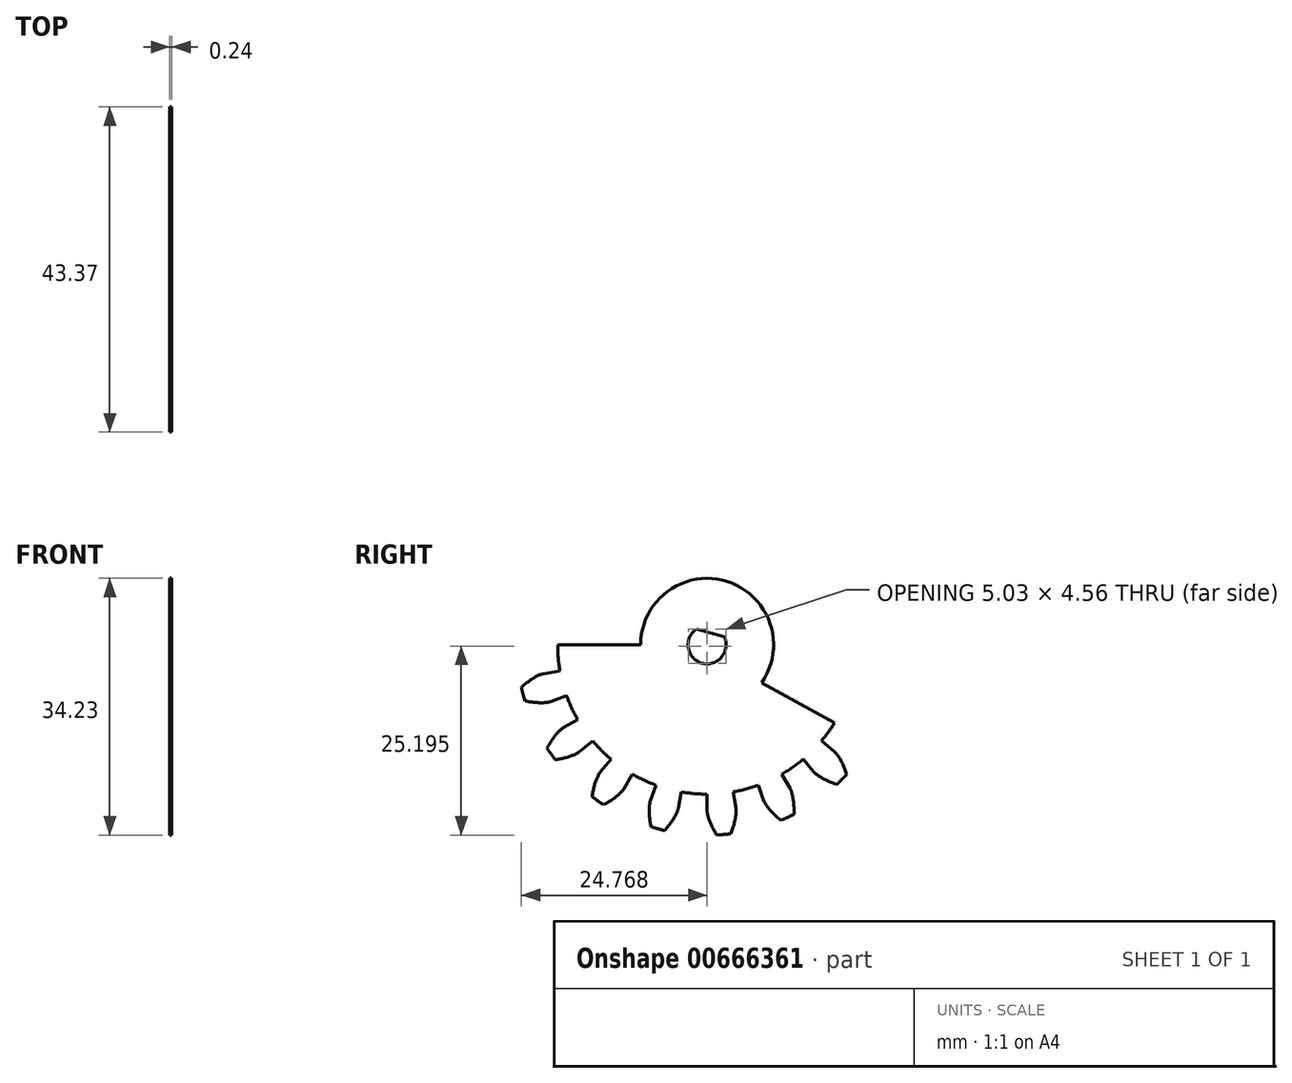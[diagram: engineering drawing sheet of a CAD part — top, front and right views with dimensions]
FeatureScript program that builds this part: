
annotation { "Feature Type Name" : "Feature", "Feature Type Description" : "" }
export const myFeature = defineFeature(function(context is Context, id is Id, definition is map)
    precondition{}
    {
        {
            assignVariable(context, id + "F0", {"name" : "NumberTeeth", "anyValue" : 18});
        }
        {
            assignVariable(context, id + "F1", {"name" : "GearThickness", "anyValue" : .236});
        }
        {
            var Q0;
            Q0=qCreatedBy(makeId("Right.planeOp"),FACE);
            var sketch = newSketch(context, id + "F2", { "sketchPlane" : qUnion([Q0])});
            skCircle(sketch, "E0", {"center": v(0, 0) * mm, "radius": 19.92 * mm});
            skCircle(sketch, "E1", {"center": v(0, 0) * mm, "radius": 22.13 * mm, "construction": true});
            skCircle(sketch, "E2", {"center": v(0, 0) * mm, "radius": 22.86 * mm, "construction": true});
            skCircle(sketch, "E3", {"center": v(0, 0) * mm, "radius": 25.4 * mm});
            skLineSegment(sketch, "E4", {"start": v(0, 0) * mm, "end": v(-22.13, 0) * mm, "construction": true});
            skLineSegment(sketch, "E5.1.0", {"start": v(0, 0) * mm, "end": v(-22.1, 1.1) * mm, "construction": true});
            skLineSegment(sketch, "E5.2.0", {"start": v(0, 0) * mm, "end": v(-22.02, 2.2) * mm, "construction": true});
            skLineSegment(sketch, "E5.3.0", {"start": v(0, 0) * mm, "end": v(-21.88, 3.3) * mm, "construction": true});
            skLineSegment(sketch, "E5.4.0", {"start": v(0, 0) * mm, "end": v(-21.7, 4.4) * mm, "construction": true});
            skLineSegment(sketch, "E5.5.0", {"start": v(0, 0) * mm, "end": v(-21.44, 5.48) * mm, "construction": true});
            skLineSegment(sketch, "E5.6.0", {"start": v(0, 0) * mm, "end": v(-21.14, 6.54) * mm, "construction": true});
            skLineSegment(sketch, "E5.7.0", {"start": v(0, 0) * mm, "end": v(-20.8, 7.59) * mm, "construction": true});
            skLineSegment(sketch, "E5.8.0", {"start": v(0, 0) * mm, "end": v(-20.38, 8.62) * mm, "construction": true});
            skLineSegment(sketch, "E5.9.0", {"start": v(0, 0) * mm, "end": v(-19.93, 9.63) * mm, "construction": true});
            skLineSegment(sketch, "E5.10.0", {"start": v(0, 0) * mm, "end": v(-19.42, 10.61) * mm, "construction": true});
            skLineSegment(sketch, "E5.11.0", {"start": v(0, 0) * mm, "end": v(-18.87, 11.57) * mm, "construction": true});
            skLineSegment(sketch, "E5.12.0", {"start": v(0, 0) * mm, "end": v(-18.27, 12.5) * mm, "construction": true});
            skLineSegment(sketch, "E5.13.0", {"start": v(0, 0) * mm, "end": v(-17.62, 13.4) * mm, "construction": true});
            skLineSegment(sketch, "E5.14.0", {"start": v(0, 0) * mm, "end": v(-16.93, 14.26) * mm, "construction": true});
            skLineSegment(sketch, "E5.anchor2", {"start": v(0, 0) * mm, "end": v(-16.93, 14.26) * mm, "construction": true});
            skLineSegment(sketch, "E6", {"start": v(-22.1, 1.1) * mm, "end": v(-22.16, 0) * mm, "construction": true});
            skLineSegment(sketch, "E7", {"start": v(-22.02, 2.2) * mm, "end": v(-22.24, 0) * mm, "construction": true});
            skLineSegment(sketch, "E8", {"start": v(-21.88, 3.3) * mm, "end": v(-22.38, 0.02) * mm, "construction": true});
            skLineSegment(sketch, "E9", {"start": v(-21.44, 5.48) * mm, "end": v(-22.81, 0.11) * mm, "construction": true});
            skLineSegment(sketch, "E10", {"start": v(-21.14, 6.54) * mm, "end": v(-23.1, 0.2) * mm, "construction": true});
            skLineSegment(sketch, "E11", {"start": v(-20.8, 7.59) * mm, "end": v(-23.45, 0.31) * mm, "construction": true});
            skLineSegment(sketch, "E12", {"start": v(-20.38, 8.62) * mm, "end": v(-23.83, 0.46) * mm, "construction": true});
            skLineSegment(sketch, "E13", {"start": v(-19.93, 9.63) * mm, "end": v(-24.26, 0.66) * mm, "construction": true});
            skLineSegment(sketch, "E14", {"start": v(-19.42, 10.61) * mm, "end": v(-24.73, 0.9) * mm, "construction": true});
            skLineSegment(sketch, "E15", {"start": v(-18.87, 11.57) * mm, "end": v(-25.23, 1.2) * mm, "construction": true});
            skLineSegment(sketch, "E16", {"start": v(-21.7, 4.4) * mm, "end": v(-22.57, 0.06) * mm, "construction": true});
            skLineSegment(sketch, "E17", {"start": v(-18.27, 12.5) * mm, "end": v(-25.76, 1.54) * mm, "construction": true});
            skLineSegment(sketch, "E18", {"start": v(-17.62, 13.4) * mm, "end": v(-26.32, 1.94) * mm, "construction": true});
            skLineSegment(sketch, "E19", {"start": v(-16.93, 14.26) * mm, "end": v(-26.9, 2.4) * mm, "construction": true});
            skLineSegment(sketch, "E20", {"start": v(0, 0) * mm, "end": v(-22.05, 1.93) * mm, "construction": true});
            skLineSegment(sketch, "E21", {"start": v(-19.92, 0) * mm, "end": v(-22.13, 0) * mm});
            skLineSegment(sketch, "E22.MirrorCS", {"start": v(-19.62, 3.46) * mm, "end": v(-21.8, 3.84) * mm});
            skFitSpline(sketch, "E23", {"points": [v(-22.13, 0) * mm, v(-22.16, 0) * mm, v(-22.24, 0) * mm, v(-22.38, 0.02) * mm, v(-22.57, 0.06) * mm, v(-22.81, 0.11) * mm, v(-23.1, 0.2) * mm, v(-23.45, 0.31) * mm, v(-23.83, 0.46) * mm, v(-24.26, 0.66) * mm, v(-24.73, 0.9) * mm, v(-25.23, 1.2) * mm, v(-25.76, 1.54) * mm, v(-26.32, 1.94) * mm, v(-26.9, 2.4) * mm], "startDerivative": vector(-0.77, 0) * mm, "endDerivative": vector(-1.38, 1.16) * mm});
            skLineSegment(sketch, "E24", {"start": v(-22.09, -1.65) * mm, "end": v(-26.9, 2.4) * mm, "construction": true});
            skFitSpline(sketch, "E25.MirrorCS", {"points": [v(-21.8, 3.84) * mm, v(-21.82, 3.85) * mm, v(-21.9, 3.86) * mm, v(-22.04, 3.86) * mm, v(-22.24, 3.86) * mm, v(-22.49, 3.85) * mm, v(-22.79, 3.82) * mm, v(-23.14, 3.76) * mm, v(-23.55, 3.68) * mm, v(-24, 3.56) * mm, v(-24.5, 3.4) * mm, v(-25.05, 3.2) * mm, v(-25.64, 2.96) * mm, v(-26.26, 2.66) * mm, v(-26.92, 2.3) * mm], "startDerivative": vector(-0.76, 0.13) * mm, "endDerivative": vector(-1.56, -0.9) * mm});
            skSolve(sketch);
        }
        {
            var Q0;
            {var subQ0=sQuery(id+"F2.wireOp",EDGE,"E0");var subQ27=makeQuery(id+"F2.imprint","INTERSECT",VERTEX,{"derivedFrom":[subQ0,sQuery(id+"F2.wireOp",EDGE,"10ea1024-8cf5-41f5-a75f-a634b86921f3.10.0")]});Q0=makeQuery(id+"F2.imprint","IMPRINT",FACE,{"disambiguationData":[TD([[makeQuery(id+"F2.imprint","IMPRINT",EDGE,{"disambiguationData":[TD([[subQ27,-1.0]])],"derivedFrom":subQ0}),1.0]])]});}
            var Q1;
            {var subQ0=sQuery(id+"F2.wireOp",EDGE,"10ea1024-8cf5-41f5-a75f-a634b86921f3.1.0");Q1=makeQuery(id+"F2.imprint","IMPRINT",FACE,{"disambiguationData":[TD([[makeQuery(id+"F2.imprint","IMPRINT",EDGE,{"derivedFrom":subQ0}),-1.0]])]});}
            var Q2;
            {var subQ7=sQuery(id+"F2.wireOp",EDGE,"10ea1024-8cf5-41f5-a75f-a634b86921f3.2.0");Q2=makeQuery(id+"F2.imprint","IMPRINT",FACE,{"disambiguationData":[TD([[makeQuery(id+"F2.imprint","IMPRINT",EDGE,{"derivedFrom":subQ7}),-1.0]])]});}
            var Q3;
            {var subQ8=sQuery(id+"F2.wireOp",EDGE,"10ea1024-8cf5-41f5-a75f-a634b86921f3.3.0");Q3=makeQuery(id+"F2.imprint","IMPRINT",FACE,{"disambiguationData":[TD([[makeQuery(id+"F2.imprint","IMPRINT",EDGE,{"derivedFrom":subQ8}),-1.0]])]});}
            var Q4;
            {var subQ2=sQuery(id+"F2.wireOp",EDGE,"10ea1024-8cf5-41f5-a75f-a634b86921f3.4.0");Q4=makeQuery(id+"F2.imprint","IMPRINT",FACE,{"disambiguationData":[TD([[makeQuery(id+"F2.imprint","IMPRINT",EDGE,{"derivedFrom":subQ2}),-1.0]])]});}
            var Q5;
            {var subQ8=sQuery(id+"F2.wireOp",EDGE,"10ea1024-8cf5-41f5-a75f-a634b86921f3.5.0");Q5=makeQuery(id+"F2.imprint","IMPRINT",FACE,{"disambiguationData":[TD([[makeQuery(id+"F2.imprint","IMPRINT",EDGE,{"derivedFrom":subQ8}),-1.0]])]});}
            var Q6;
            {var subQ3=sQuery(id+"F2.wireOp",EDGE,"10ea1024-8cf5-41f5-a75f-a634b86921f3.6.0");Q6=makeQuery(id+"F2.imprint","IMPRINT",FACE,{"disambiguationData":[TD([[makeQuery(id+"F2.imprint","IMPRINT",EDGE,{"derivedFrom":subQ3}),-1.0]])]});}
            var Q7;
            {var subQ0=sQuery(id+"F2.wireOp",EDGE,"10ea1024-8cf5-41f5-a75f-a634b86921f3.7.0");Q7=makeQuery(id+"F2.imprint","IMPRINT",FACE,{"disambiguationData":[TD([[makeQuery(id+"F2.imprint","IMPRINT",EDGE,{"derivedFrom":subQ0}),-1.0]])]});}
            var Q8;
            {var subQ5=sQuery(id+"F2.wireOp",EDGE,"10ea1024-8cf5-41f5-a75f-a634b86921f3.8.0");Q8=makeQuery(id+"F2.imprint","IMPRINT",FACE,{"disambiguationData":[TD([[makeQuery(id+"F2.imprint","IMPRINT",EDGE,{"derivedFrom":subQ5}),-1.0]])]});}
            var Q9;
            {var subQ1=sQuery(id+"F2.wireOp",EDGE,"10ea1024-8cf5-41f5-a75f-a634b86921f3.9.0");Q9=makeQuery(id+"F2.imprint","IMPRINT",FACE,{"disambiguationData":[TD([[makeQuery(id+"F2.imprint","IMPRINT",EDGE,{"derivedFrom":subQ1}),-1.0]])]});}
            var Q10;
            {var subQ5=sQuery(id+"F2.wireOp",EDGE,"10ea1024-8cf5-41f5-a75f-a634b86921f3.10.0");Q10=makeQuery(id+"F2.imprint","IMPRINT",FACE,{"disambiguationData":[TD([[makeQuery(id+"F2.imprint","IMPRINT",EDGE,{"derivedFrom":subQ5}),-1.0]])]});}
            var Q11;
            {var subQ8=sQuery(id+"F2.wireOp",EDGE,"10ea1024-8cf5-41f5-a75f-a634b86921f3.11.0");Q11=makeQuery(id+"F2.imprint","IMPRINT",FACE,{"disambiguationData":[TD([[makeQuery(id+"F2.imprint","IMPRINT",EDGE,{"derivedFrom":subQ8}),-1.0]])]});}
            var Q12;
            {var subQ2=sQuery(id+"F2.wireOp",EDGE,"10ea1024-8cf5-41f5-a75f-a634b86921f3.12.0");Q12=makeQuery(id+"F2.imprint","IMPRINT",FACE,{"disambiguationData":[TD([[makeQuery(id+"F2.imprint","IMPRINT",EDGE,{"derivedFrom":subQ2}),-1.0]])]});}
            var Q13;
            {var subQ3=sQuery(id+"F2.wireOp",EDGE,"10ea1024-8cf5-41f5-a75f-a634b86921f3.13.0");Q13=makeQuery(id+"F2.imprint","IMPRINT",FACE,{"disambiguationData":[TD([[makeQuery(id+"F2.imprint","IMPRINT",EDGE,{"derivedFrom":subQ3}),-1.0]])]});}
            var Q14;
            {var subQ0=sQuery(id+"F2.wireOp",EDGE,"10ea1024-8cf5-41f5-a75f-a634b86921f3.14.0");Q14=makeQuery(id+"F2.imprint","IMPRINT",FACE,{"disambiguationData":[TD([[makeQuery(id+"F2.imprint","IMPRINT",EDGE,{"derivedFrom":subQ0}),-1.0]])]});}
            var Q15;
            {var subQ6=sQuery(id+"F2.wireOp",EDGE,"10ea1024-8cf5-41f5-a75f-a634b86921f3.15.0");Q15=makeQuery(id+"F2.imprint","IMPRINT",FACE,{"disambiguationData":[TD([[makeQuery(id+"F2.imprint","IMPRINT",EDGE,{"derivedFrom":subQ6}),-1.0]])]});}
            var Q16;
            {var subQ5=sQuery(id+"F2.wireOp",EDGE,"10ea1024-8cf5-41f5-a75f-a634b86921f3.16.0");Q16=makeQuery(id+"F2.imprint","IMPRINT",FACE,{"disambiguationData":[TD([[makeQuery(id+"F2.imprint","IMPRINT",EDGE,{"derivedFrom":subQ5}),-1.0]])]});}
            var Q17;
            {var subQ7=sQuery(id+"F2.wireOp",EDGE,"10ea1024-8cf5-41f5-a75f-a634b86921f3.17.0");Q17=makeQuery(id+"F2.imprint","IMPRINT",FACE,{"disambiguationData":[TD([[makeQuery(id+"F2.imprint","IMPRINT",EDGE,{"derivedFrom":subQ7}),-1.0]])]});}
            var Q18;
            {var subQ5=sQuery(id+"F2.wireOp",EDGE,"10ea1024-8cf5-41f5-a75f-a634b86921f3.18.0");Q18=makeQuery(id+"F2.imprint","IMPRINT",FACE,{"disambiguationData":[TD([[makeQuery(id+"F2.imprint","IMPRINT",EDGE,{"derivedFrom":subQ5}),-1.0]])]});}
            var Q19;
            {var subQ8=sQuery(id+"F2.wireOp",EDGE,"10ea1024-8cf5-41f5-a75f-a634b86921f3.19.0");Q19=makeQuery(id+"F2.imprint","IMPRINT",FACE,{"disambiguationData":[TD([[makeQuery(id+"F2.imprint","IMPRINT",EDGE,{"derivedFrom":subQ8}),-1.0]])]});}
            var Q20;
            {var subQ8=sQuery(id+"F2.wireOp",EDGE,"E21");Q20=makeQuery(id+"F2.imprint","IMPRINT",FACE,{"disambiguationData":[TD([[makeQuery(id+"F2.imprint","IMPRINT",EDGE,{"derivedFrom":subQ8}),-1.0]])]});}
            extrude(context, id + "F3", {"entities" : qUnion([Q0, Q1, Q2, Q3, Q4, Q5, Q6, Q7, Q8, Q9, Q10, Q11, Q12, Q13, Q14, Q15, Q16, Q17, Q18, Q19, Q20]), "depth" : (getVariable(context, 'GearThickness')) * mm});
        }
        {
            var Q0;
            Q0=makeQuery(id+"F3.opExtrude","SWEPT_FACE",FACE,{"disambiguationData":[OSD([sQuery(id+"F2.wireOp",EDGE,"E25.MirrorCS")])]});
            var Q1;
            Q1=makeQuery(id+"F3.opExtrude","SWEPT_FACE",FACE,{"disambiguationData":[OSD([sQuery(id+"F2.wireOp",EDGE,"E23")])]});
            var Q2;
            Q2=makeQuery(id+"F3.opExtrude","SWEPT_FACE",FACE,{"disambiguationData":[OSD([sQuery(id+"F2.wireOp",EDGE,"E3")])]});
            var Q3;
            Q3=makeQuery(id+"F3.opExtrude","SWEPT_FACE",FACE,{"disambiguationData":[OSD([sQuery(id+"F2.wireOp",EDGE,"E22.MirrorCS")])]});
            var Q4;
            Q4=makeQuery(id+"F3.opExtrude","SWEPT_FACE",FACE,{"disambiguationData":[OSD([sQuery(id+"F2.wireOp",EDGE,"E21")])]});
            var Q5;
            Q5=makeQuery(id+"F3.opExtrude","SWEPT_FACE",FACE,{"disambiguationData":[OSD([sQuery(id+"F2.wireOp",EDGE,"E0")])]});
            circularPattern(context, id + "F4", {"faces" : qUnion([Q0, Q1, Q2, Q3, Q4]), "axis" : qUnion([Q5]), "angle" : 360 * degree, "instanceCount" : getVariable(context, 'NumberTeeth'), "equalSpace" : true, "patternType" : PatternType.FACE});
        }
        {
            var Q0;
            Q0=qCreatedBy(makeId("Right.planeOp"),FACE);
            var sketch = newSketch(context, id + "F5", { "sketchPlane" : qUnion([Q0])});
            skLineSegment(sketch, "E26", {"start": v(0, 0) * mm, "end": v(-6.74, -25.1) * mm, "construction": true});
            skLineSegment(sketch, "E27", {"start": v(0, 0) * mm, "end": v(25.01, -6.72) * mm, "construction": true});
            skSolve(sketch);
        }
        {
            var Q0;
            Q0=sQuery(id+"F5.wireOp",EDGE,"E27");
            cPlane(context, id + "F6", {"entities" : qUnion([Q0]), "cplaneType" : CPlaneType.LINE_ANGLE, "offset" : 25.4 * mm, "angle" : 0 * degree, "width" : 152.4 * mm, "height" : 152.4 * mm});
        }
        {
            var Q0;
            Q0=qCreatedBy(makeId("Right.planeOp"),FACE);
            var sketch = newSketch(context, id + "F7", { "sketchPlane" : qUnion([Q0])});
            skCircle(sketch, "E28", {"center": v(0, 0) * mm, "radius": 2.54 * mm});
            skLineSegment(sketch, "E29", {"start": v(2.29, 1.1) * mm, "end": v(-1.42, 2.1) * mm});
            skSolve(sketch);
        }
        {
            var Q0;
            {var subQ0=sQuery(id+"F7.wireOp",EDGE,"E29");Q0=makeQuery(id+"F7.imprint","IMPRINT",FACE,{"disambiguationData":[TD([[makeQuery(id+"F7.imprint","IMPRINT",EDGE,{"derivedFrom":subQ0}),1.0]])]});}
            extrude(context, id + "F8", {"entities" : qUnion([Q0]), "operationType" : NewBodyOperationType.REMOVE, "depth" : 25.4 * mm, "offsetDistance" : 25.4 * mm});
        }
        {
            var Q0;
            Q0=makeQuery(id+"F3.opExtrude","CAP_FACE",FACE,{"disambiguationData":[OSD([sQuery(id+"F2.wireOp",EDGE,"E0"),sQuery(id+"F2.wireOp",EDGE,"E3"),sQuery(id+"F2.wireOp",EDGE,"E21"),sQuery(id+"F2.wireOp",EDGE,"E22.MirrorCS"),sQuery(id+"F2.wireOp",EDGE,"E23"),sQuery(id+"F2.wireOp",EDGE,"E25.MirrorCS")])],"isStart":false});
            var sketch = newSketch(context, id + "F9", { "sketchPlane" : qUnion([Q0])});
            skLineSegment(sketch, "E30", {"start": v(0, 19.92) * mm, "end": v(3.46, 19.62) * mm, "construction": true});
            skSolve(sketch);
        }
        {
            var Q0;
            Q0=qCreatedBy(id+"F6.planeOp",FACE);
            var sketch = newSketch(context, id + "F10", { "sketchPlane" : qUnion([Q0])});
            skCircle(sketch, "E31", {"center": v(3, 0) * mm, "radius": 1.5 * mm});
            skSolve(sketch);
        }
        {
            var Q0;
            Q0 = qSketchRegion(id + "F10", true);
            extrude(context, id + "F11", {"entities" : qUnion([Q0]), "operationType" : NewBodyOperationType.REMOVE, "depth" : 43.18 * mm, "offsetDistance" : 25.4 * mm});
        }
        {
            var Q0;
            {var subQ10=sQuery(id+"F2.wireOp",EDGE,"E3");var subQ11=makeQuery(id+"F3.opExtrude","CAP_EDGE",EDGE,{"disambiguationData":[OSD([subQ10])],"isStart":false});Q0=makeQuery(id+"F9.imprint","IMPRINT",FACE,{"disambiguationData":[TD([[makeQuery(id+"F9.imprint","IMPRINT",EDGE,{"derivedFrom":subQ11}),1.0]])]});}
            var sketch = newSketch(context, id + "F12", { "sketchPlane" : qUnion([Q0])});
            skArc(sketch, "E32", {"start": v(-29.86, 0) * mm, "mid": v(7.88, 28.8) * mm, "end": v(25.7, -15.2) * mm});
            skArc(sketch, "E33", {"start": v(-8.86, 0) * mm, "mid": v(2.65, 8.46) * mm, "end": v(7.27, -5.06) * mm});
            skLineSegment(sketch, "E34", {"start": v(7.27, -5.06) * mm, "end": v(25.7, -15.2) * mm});
            skLineSegment(sketch, "E35", {"start": v(-8.86, 0) * mm, "end": v(-29.86, 0) * mm});
            skSolve(sketch);
        }
        {
            var Q0;
            Q0 = qSketchRegion(id + "F12", true);
            extrude(context, id + "F13", {"entities" : qUnion([Q0]), "operationType" : NewBodyOperationType.REMOVE, "oppositeDirection" : true, "depth" : 25.4 * mm, "offsetDistance" : 25.4 * mm});
        }
    });
